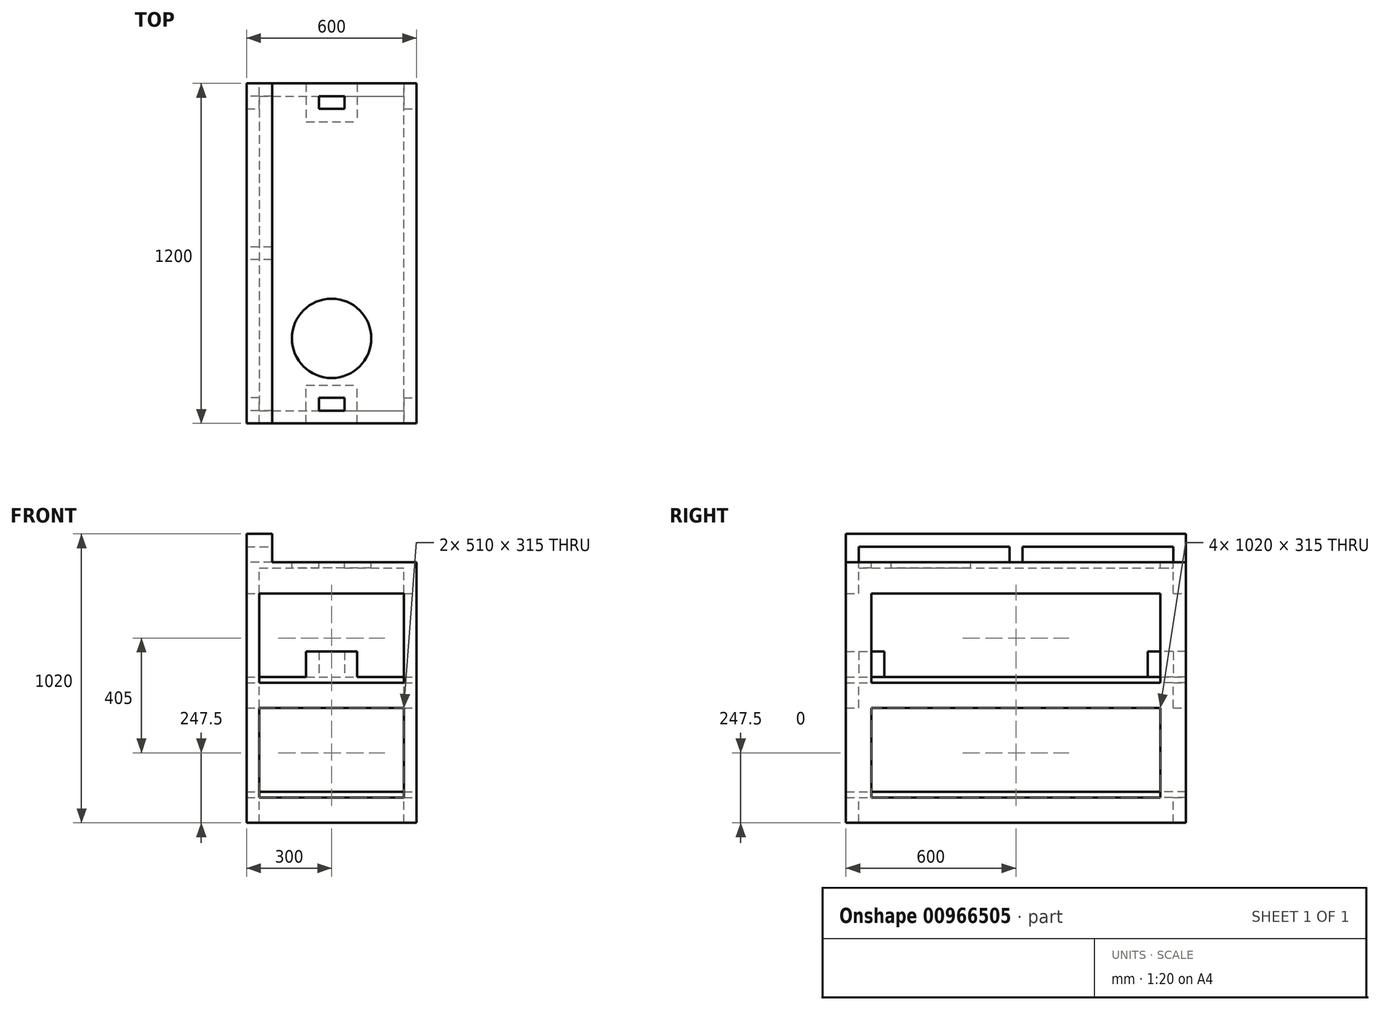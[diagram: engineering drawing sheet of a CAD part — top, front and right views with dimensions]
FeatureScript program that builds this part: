
annotation { "Feature Type Name" : "Feature", "Feature Type Description" : "" }
export const myFeature = defineFeature(function(context is Context, id is Id, definition is map)
    precondition{}
    {
        {
            var Q0;
            Q0=qCreatedBy(makeId("Top.planeOp"),FACE);
            var sketch = newSketch(context, id + "F0", { "sketchPlane" : qUnion([Q0])});
            skLineSegment(sketch, "E0.bottom", {"start": v(0, 0) * mm, "end": v(-600, 0) * mm});
            skLineSegment(sketch, "E0.top", {"start": v(0, 1200) * mm, "end": v(-600, 1200) * mm});
            skLineSegment(sketch, "E0.left", {"start": v(0, 0) * mm, "end": v(0, 1200) * mm});
            skLineSegment(sketch, "E0.right", {"start": v(-600, 0) * mm, "end": v(-600, 1200) * mm});
            skSolve(sketch);
        }
        {
            var Q0;
            Q0 = qSketchRegion(id + "F0", true);
            extrude(context, id + "F1", {"entities" : qUnion([Q0]), "depth" : 900 * mm, "offsetDistance" : 25 * mm});
        }
        {
            var Q0;
            Q0=makeQuery(id+"F1.opExtrude","CAP_FACE",FACE,{"disambiguationData":[OSD([sQuery(id+"F0.wireOp",EDGE,"E0.bottom"),sQuery(id+"F0.wireOp",EDGE,"E0.top"),sQuery(id+"F0.wireOp",EDGE,"E0.left"),sQuery(id+"F0.wireOp",EDGE,"E0.right")])],"isStart":false});
            var sketch = newSketch(context, id + "F2", { "sketchPlane" : qUnion([Q0])});
            skLineSegment(sketch, "E1", {"start": v(0, 600) * mm, "end": v(-600, 600) * mm, "construction": true});
            skLineSegment(sketch, "E2", {"start": v(-300, 0) * mm, "end": v(-300, 1200) * mm, "construction": true});
            skLineSegment(sketch, "E3", {"start": v(-300, 45) * mm, "end": v(-45, 45) * mm});
            skLineSegment(sketch, "E4", {"start": v(-45, 45) * mm, "end": v(-45, 600) * mm});
            skLineSegment(sketch, "E5.MirrorCS", {"start": v(-300, 1155) * mm, "end": v(-45, 1155) * mm});
            skLineSegment(sketch, "E6.MirrorCS", {"start": v(-45, 1155) * mm, "end": v(-45, 600) * mm});
            skLineSegment(sketch, "E7.MirrorCS", {"start": v(-300, 1200) * mm, "end": v(-300, 0) * mm, "construction": true});
            skLineSegment(sketch, "E8.MirrorCS", {"start": v(-300, 1155) * mm, "end": v(-555, 1155) * mm});
            skLineSegment(sketch, "E9.MirrorCS", {"start": v(-555, 1155) * mm, "end": v(-555, 600) * mm});
            skLineSegment(sketch, "E10.MirrorCS", {"start": v(-300, 45) * mm, "end": v(-555, 45) * mm});
            skLineSegment(sketch, "E11.MirrorCS", {"start": v(-555, 45) * mm, "end": v(-555, 600) * mm});
            skSolve(sketch);
        }
        {
            var Q0;
            Q0 = qSketchRegion(id + "F2", true);
            extrude(context, id + "F3", {"entities" : qUnion([Q0]), "operationType" : NewBodyOperationType.REMOVE, "endBound" : BoundingType.THROUGH_ALL, "oppositeDirection" : true, "depth" : 25 * mm, "offsetDistance" : 25 * mm});
        }
        {
            var Q0;
            Q0=makeQuery(id+"F1.opExtrude","SWEPT_FACE",FACE,{"disambiguationData":[OSD([sQuery(id+"F0.wireOp",EDGE,"E0.left")])]});
            var sketch = newSketch(context, id + "F4", { "sketchPlane" : qUnion([Q0])});
            skLineSegment(sketch, "E12.bottom", {"start": v(90, 810) * mm, "end": v(1110, 810) * mm});
            skLineSegment(sketch, "E12.top", {"start": v(90, 495) * mm, "end": v(1110, 495) * mm});
            skLineSegment(sketch, "E12.left", {"start": v(90, 810) * mm, "end": v(90, 495) * mm});
            skLineSegment(sketch, "E12.right", {"start": v(1110, 810) * mm, "end": v(1110, 495) * mm});
            skLineSegment(sketch, "E13.bottom", {"start": v(90, 405) * mm, "end": v(1110, 405) * mm});
            skLineSegment(sketch, "E13.top", {"start": v(90, 90) * mm, "end": v(1110, 90) * mm});
            skLineSegment(sketch, "E13.left", {"start": v(90, 405) * mm, "end": v(90, 90) * mm});
            skLineSegment(sketch, "E13.right", {"start": v(1110, 405) * mm, "end": v(1110, 90) * mm});
            skSolve(sketch);
        }
        {
            var Q0;
            Q0 = qSketchRegion(id + "F4", true);
            extrude(context, id + "F5", {"entities" : qUnion([Q0]), "operationType" : NewBodyOperationType.REMOVE, "endBound" : BoundingType.THROUGH_ALL, "oppositeDirection" : true, "depth" : 25 * mm, "offsetDistance" : 25 * mm});
        }
        {
            var Q0;
            Q0=makeQuery(id+"F1.opExtrude","SWEPT_FACE",FACE,{"disambiguationData":[OSD([sQuery(id+"F0.wireOp",EDGE,"E0.top")])]});
            var sketch = newSketch(context, id + "F6", { "sketchPlane" : qUnion([Q0])});
            skLineSegment(sketch, "E14.bottom", {"start": v(45, 810) * mm, "end": v(555, 810) * mm});
            skLineSegment(sketch, "E14.top", {"start": v(45, 495) * mm, "end": v(555, 495) * mm});
            skLineSegment(sketch, "E14.left", {"start": v(45, 810) * mm, "end": v(45, 495) * mm});
            skLineSegment(sketch, "E14.right", {"start": v(555, 810) * mm, "end": v(555, 495) * mm});
            skLineSegment(sketch, "E15.bottom", {"start": v(45, 405) * mm, "end": v(555, 405) * mm});
            skLineSegment(sketch, "E15.top", {"start": v(45, 90) * mm, "end": v(555, 90) * mm});
            skLineSegment(sketch, "E15.left", {"start": v(45, 405) * mm, "end": v(45, 90) * mm});
            skLineSegment(sketch, "E15.right", {"start": v(555, 405) * mm, "end": v(555, 90) * mm});
            skSolve(sketch);
        }
        {
            var Q0;
            Q0 = qSketchRegion(id + "F6", true);
            extrude(context, id + "F7", {"entities" : qUnion([Q0]), "operationType" : NewBodyOperationType.REMOVE, "endBound" : BoundingType.THROUGH_ALL, "oppositeDirection" : true, "depth" : 25 * mm, "offsetDistance" : 25 * mm});
        }
        {
            var Q0;
            Q0=makeQuery(id+"F1.opExtrude","CAP_FACE",FACE,{"disambiguationData":[OSD([sQuery(id+"F0.wireOp",EDGE,"E0.bottom"),sQuery(id+"F0.wireOp",EDGE,"E0.top"),sQuery(id+"F0.wireOp",EDGE,"E0.left"),sQuery(id+"F0.wireOp",EDGE,"E0.right")])],"isStart":false});
            var sketch = newSketch(context, id + "F8", { "sketchPlane" : qUnion([Q0])});
            skLineSegment(sketch, "E16.bottom", {"start": v(0, 0) * mm, "end": v(-600, 0) * mm});
            skLineSegment(sketch, "E16.top", {"start": v(0, 1200) * mm, "end": v(-600, 1200) * mm});
            skLineSegment(sketch, "E16.left", {"start": v(0, 0) * mm, "end": v(0, 1200) * mm});
            skLineSegment(sketch, "E16.right", {"start": v(-600, 0) * mm, "end": v(-600, 1200) * mm});
            skSolve(sketch);
        }
        {
            var Q0;
            Q0 = qSketchRegion(id + "F8", true);
            extrude(context, id + "F9", {"entities" : qUnion([Q0]), "depth" : 20 * mm, "offsetDistance" : 25 * mm});
        }
        {
            var Q0;
            Q0=makeQuery(id+"F5.boolean.opBoolean","COPY",FACE,{"disambiguationData":[TD([makeQuery(id+"F1.opExtrude","SWEPT_FACE",FACE,{"disambiguationData":[OSD([sQuery(id+"F0.wireOp",EDGE,"E0.left")])]})])],"derivedFrom":makeQuery(id+"F5.opExtrude","SWEPT_FACE",FACE,{"disambiguationData":[OSD([sQuery(id+"F4.wireOp",EDGE,"E12.top")])]})});
            var sketch = newSketch(context, id + "F10", { "sketchPlane" : qUnion([Q0])});
            skLineSegment(sketch, "E17", {"start": v(0, 90) * mm, "end": v(-45, 90) * mm});
            skLineSegment(sketch, "E18", {"start": v(-45, 90) * mm, "end": v(-45, 0) * mm});
            skLineSegment(sketch, "E19", {"start": v(-45, 0) * mm, "end": v(-555, 0) * mm});
            skLineSegment(sketch, "E20", {"start": v(-555, 0) * mm, "end": v(-555, 90) * mm});
            skLineSegment(sketch, "E21", {"start": v(-555, 90) * mm, "end": v(-600, 90) * mm});
            skLineSegment(sketch, "E22", {"start": v(-600, 90) * mm, "end": v(-600, 1110) * mm});
            skLineSegment(sketch, "E23", {"start": v(-600, 1110) * mm, "end": v(-555, 1110) * mm});
            skLineSegment(sketch, "E24", {"start": v(-555, 1110) * mm, "end": v(-555, 1200) * mm});
            skLineSegment(sketch, "E25", {"start": v(-555, 1200) * mm, "end": v(-45, 1200) * mm});
            skLineSegment(sketch, "E26", {"start": v(-45, 1200) * mm, "end": v(-45, 1110) * mm});
            skLineSegment(sketch, "E27", {"start": v(-45, 1110) * mm, "end": v(0, 1110) * mm});
            skLineSegment(sketch, "E28", {"start": v(0, 1110) * mm, "end": v(0, 90) * mm});
            skSolve(sketch);
        }
        {
            var Q0;
            Q0 = qSketchRegion(id + "F10", true);
            extrude(context, id + "F11", {"entities" : qUnion([Q0]), "depth" : 20 * mm, "offsetDistance" : 25 * mm});
        }
        {
            var Q0;
            Q0=makeQuery(id+"F5.boolean.opBoolean","COPY",FACE,{"disambiguationData":[TD([makeQuery(id+"F1.opExtrude","SWEPT_FACE",FACE,{"disambiguationData":[OSD([sQuery(id+"F0.wireOp",EDGE,"E0.left")])]})])],"derivedFrom":makeQuery(id+"F5.opExtrude","SWEPT_FACE",FACE,{"disambiguationData":[OSD([sQuery(id+"F4.wireOp",EDGE,"E13.top")])]})});
            var sketch = newSketch(context, id + "F12", { "sketchPlane" : qUnion([Q0])});
            skLineSegment(sketch, "E29", {"start": v(0, 90) * mm, "end": v(-45, 90) * mm});
            skLineSegment(sketch, "E30", {"start": v(-45, 90) * mm, "end": v(-45, 0) * mm});
            skLineSegment(sketch, "E31", {"start": v(-45, 0) * mm, "end": v(-555, 0) * mm});
            skLineSegment(sketch, "E32", {"start": v(-555, 0) * mm, "end": v(-555, 90) * mm});
            skLineSegment(sketch, "E33", {"start": v(-555, 90) * mm, "end": v(-600, 90) * mm});
            skLineSegment(sketch, "E34", {"start": v(-600, 90) * mm, "end": v(-600, 1110) * mm});
            skLineSegment(sketch, "E35", {"start": v(-600, 1110) * mm, "end": v(-555, 1110) * mm});
            skLineSegment(sketch, "E36", {"start": v(-555, 1110) * mm, "end": v(-555, 1200) * mm});
            skLineSegment(sketch, "E37", {"start": v(-555, 1200) * mm, "end": v(-45, 1200) * mm});
            skLineSegment(sketch, "E38", {"start": v(-45, 1200) * mm, "end": v(-45, 1110) * mm});
            skLineSegment(sketch, "E39", {"start": v(-45, 1110) * mm, "end": v(0, 1110) * mm});
            skLineSegment(sketch, "E40", {"start": v(0, 1110) * mm, "end": v(0, 90) * mm});
            skSolve(sketch);
        }
        {
            var Q0;
            Q0 = qSketchRegion(id + "F12", true);
            extrude(context, id + "F13", {"entities" : qUnion([Q0]), "depth" : 20 * mm, "offsetDistance" : 25 * mm});
        }
        {
            var Q0;
            Q0=makeQuery(id+"F9.opExtrude","CAP_FACE",FACE,{"disambiguationData":[OSD([sQuery(id+"F8.wireOp",EDGE,"E16.bottom"),sQuery(id+"F8.wireOp",EDGE,"E16.top"),sQuery(id+"F8.wireOp",EDGE,"E16.left"),sQuery(id+"F8.wireOp",EDGE,"E16.right")])],"isStart":false});
            var sketch = newSketch(context, id + "F14", { "sketchPlane" : qUnion([Q0])});
            skCircle(sketch, "E41", {"center": v(-300, 300) * mm, "radius": 140 * mm});
            skSolve(sketch);
        }
        {
            var Q0;
            Q0 = qSketchRegion(id + "F14", true);
            extrude(context, id + "F15", {"entities" : qUnion([Q0]), "operationType" : NewBodyOperationType.REMOVE, "endBound" : BoundingType.UP_TO_NEXT, "oppositeDirection" : true, "depth" : 25 * mm, "offsetDistance" : 25 * mm});
        }
        {
            var Q0;
            Q0=makeQuery(id+"F9.opExtrude","CAP_FACE",FACE,{"disambiguationData":[OSD([sQuery(id+"F8.wireOp",EDGE,"E16.bottom"),sQuery(id+"F8.wireOp",EDGE,"E16.top"),sQuery(id+"F8.wireOp",EDGE,"E16.left"),sQuery(id+"F8.wireOp",EDGE,"E16.right")])],"isStart":false});
            var sketch = newSketch(context, id + "F16", { "sketchPlane" : qUnion([Q0])});
            skLineSegment(sketch, "E42", {"start": v(-600, 600) * mm, "end": v(0, 600) * mm, "construction": true});
            skLineSegment(sketch, "E43.bottom", {"start": v(-345, 45) * mm, "end": v(-255, 45) * mm});
            skLineSegment(sketch, "E43.top", {"start": v(-345, 90) * mm, "end": v(-255, 90) * mm});
            skLineSegment(sketch, "E43.left", {"start": v(-345, 45) * mm, "end": v(-345, 90) * mm});
            skLineSegment(sketch, "E43.right", {"start": v(-255, 45) * mm, "end": v(-255, 90) * mm});
            skPoint(sketch, "E44", {"position": v(-300, 45) * mm});
            skLineSegment(sketch, "E45.MirrorCS", {"start": v(-345, 1155) * mm, "end": v(-255, 1155) * mm});
            skPoint(sketch, "E46.MirrorP", {"position": v(-300, 1155) * mm});
            skLineSegment(sketch, "E47.MirrorCS", {"start": v(-345, 1155) * mm, "end": v(-345, 1110) * mm});
            skLineSegment(sketch, "E48.MirrorCS", {"start": v(-255, 1155) * mm, "end": v(-255, 1110) * mm});
            skLineSegment(sketch, "E49.MirrorCS", {"start": v(-345, 1110) * mm, "end": v(-255, 1110) * mm});
            skSolve(sketch);
        }
        {
            var Q0;
            Q0 = qSketchRegion(id + "F16", true);
            extrude(context, id + "F17", {"entities" : qUnion([Q0]), "operationType" : NewBodyOperationType.REMOVE, "endBound" : BoundingType.UP_TO_NEXT, "oppositeDirection" : true, "depth" : 25 * mm, "offsetDistance" : 25 * mm});
        }
        {
            var Q0;
            Q0=makeQuery(id+"F11.opExtrude","CAP_FACE",FACE,{"disambiguationData":[OSD([sQuery(id+"F10.wireOp",EDGE,"E17"),sQuery(id+"F10.wireOp",EDGE,"E18"),sQuery(id+"F10.wireOp",EDGE,"E19"),sQuery(id+"F10.wireOp",EDGE,"E20"),sQuery(id+"F10.wireOp",EDGE,"E21"),sQuery(id+"F10.wireOp",EDGE,"E22"),sQuery(id+"F10.wireOp",EDGE,"E23"),sQuery(id+"F10.wireOp",EDGE,"E24"),sQuery(id+"F10.wireOp",EDGE,"E25"),sQuery(id+"F10.wireOp",EDGE,"E26"),sQuery(id+"F10.wireOp",EDGE,"E27"),sQuery(id+"F10.wireOp",EDGE,"E28")])],"isStart":false});
            var sketch = newSketch(context, id + "F18", { "sketchPlane" : qUnion([Q0])});
            skLineSegment(sketch, "E50.bottom", {"start": v(-345, 45) * mm, "end": v(-255, 45) * mm});
            skLineSegment(sketch, "E50.top", {"start": v(-345, 90) * mm, "end": v(-255, 90) * mm});
            skLineSegment(sketch, "E50.left", {"start": v(-345, 45) * mm, "end": v(-345, 90) * mm});
            skLineSegment(sketch, "E50.right", {"start": v(-255, 45) * mm, "end": v(-255, 90) * mm});
            skPoint(sketch, "E51", {"position": v(-300, 45) * mm});
            skPoint(sketch, "E52", {"position": v(-300, 0) * mm});
            skLineSegment(sketch, "E53.bottom", {"start": v(-390, 0) * mm, "end": v(-210, 0) * mm});
            skLineSegment(sketch, "E53.top", {"start": v(-390, 135) * mm, "end": v(-210, 135) * mm});
            skLineSegment(sketch, "E53.left", {"start": v(-390, 0) * mm, "end": v(-390, 135) * mm});
            skLineSegment(sketch, "E53.right", {"start": v(-210, 0) * mm, "end": v(-210, 135) * mm});
            skLineSegment(sketch, "E54", {"start": v(0, 600) * mm, "end": v(-600, 600) * mm, "construction": true});
            skPoint(sketch, "E55.MirrorP", {"position": v(-300, 1155) * mm});
            skLineSegment(sketch, "E56.MirrorCS", {"start": v(-210, 1200) * mm, "end": v(-210, 1065) * mm});
            skLineSegment(sketch, "E57.MirrorCS", {"start": v(-345, 1155) * mm, "end": v(-345, 1110) * mm});
            skLineSegment(sketch, "E58.MirrorCS", {"start": v(-390, 1065) * mm, "end": v(-210, 1065) * mm});
            skLineSegment(sketch, "E59.MirrorCS", {"start": v(-345, 1155) * mm, "end": v(-255, 1155) * mm});
            skLineSegment(sketch, "E60.MirrorCS", {"start": v(-390, 1200) * mm, "end": v(-210, 1200) * mm});
            skPoint(sketch, "E61.MirrorP", {"position": v(-300, 1200) * mm});
            skLineSegment(sketch, "E62.MirrorCS", {"start": v(-390, 1200) * mm, "end": v(-390, 1065) * mm});
            skLineSegment(sketch, "E63.MirrorCS", {"start": v(-345, 1110) * mm, "end": v(-255, 1110) * mm});
            skLineSegment(sketch, "E64.MirrorCS", {"start": v(-255, 1155) * mm, "end": v(-255, 1110) * mm});
            skSolve(sketch);
        }
        {
            var Q0;
            Q0 = qSketchRegion(id + "F18", true);
            extrude(context, id + "F19", {"entities" : qUnion([Q0]), "operationType" : NewBodyOperationType.ADD, "depth" : 90 * mm, "offsetDistance" : 25 * mm});
        }
        {
            var Q0;
            Q0=makeQuery(id+"F1.opExtrude","CAP_FACE",FACE,{"disambiguationData":[OSD([sQuery(id+"F0.wireOp",EDGE,"E0.bottom"),sQuery(id+"F0.wireOp",EDGE,"E0.top"),sQuery(id+"F0.wireOp",EDGE,"E0.left"),sQuery(id+"F0.wireOp",EDGE,"E0.right")])],"isStart":false});
            var sketch = newSketch(context, id + "F20", { "sketchPlane" : qUnion([Q0])});
            skLineSegment(sketch, "E65.bottom", {"start": v(-600, 0) * mm, "end": v(-510, 0) * mm});
            skLineSegment(sketch, "E65.top", {"start": v(-600, 45) * mm, "end": v(-510, 45) * mm});
            skLineSegment(sketch, "E65.left", {"start": v(-600, 0) * mm, "end": v(-600, 45) * mm});
            skLineSegment(sketch, "E65.right", {"start": v(-510, 0) * mm, "end": v(-510, 45) * mm});
            skLineSegment(sketch, "E66.bottom", {"start": v(-600, 1200) * mm, "end": v(-510, 1200) * mm});
            skLineSegment(sketch, "E66.top", {"start": v(-600, 1155) * mm, "end": v(-510, 1155) * mm});
            skLineSegment(sketch, "E66.left", {"start": v(-600, 1200) * mm, "end": v(-600, 1155) * mm});
            skLineSegment(sketch, "E66.right", {"start": v(-510, 1200) * mm, "end": v(-510, 1155) * mm});
            skLineSegment(sketch, "E67.bottom", {"start": v(-600, 577.5) * mm, "end": v(-510, 577.5) * mm});
            skLineSegment(sketch, "E67.top", {"start": v(-600, 622.5) * mm, "end": v(-510, 622.5) * mm});
            skLineSegment(sketch, "E67.left", {"start": v(-600, 577.5) * mm, "end": v(-600, 622.5) * mm});
            skLineSegment(sketch, "E67.right", {"start": v(-510, 577.5) * mm, "end": v(-510, 622.5) * mm});
            skPoint(sketch, "E68", {"position": v(-510, 600) * mm});
            skLineSegment(sketch, "E69", {"start": v(-600, 600) * mm, "end": v(-510, 600) * mm, "construction": true});
            skSolve(sketch);
        }
        {
            var Q0;
            Q0 = qSketchRegion(id + "F20", true);
            extrude(context, id + "F21", {"entities" : qUnion([Q0]), "operationType" : NewBodyOperationType.ADD, "depth" : 75 * mm, "offsetDistance" : 25 * mm});
        }
        {
            var Q0;
            Q0=makeQuery(id+"F21.opExtrude","CAP_FACE",FACE,{"disambiguationData":[OSD([sQuery(id+"F20.wireOp",EDGE,"E65.bottom"),sQuery(id+"F20.wireOp",EDGE,"E65.top"),sQuery(id+"F20.wireOp",EDGE,"E65.left"),sQuery(id+"F20.wireOp",EDGE,"E65.right")])],"isStart":false});
            var sketch = newSketch(context, id + "F22", { "sketchPlane" : qUnion([Q0])});
            skLineSegment(sketch, "E70.bottom", {"start": v(-600, 0) * mm, "end": v(-510, 0) * mm});
            skLineSegment(sketch, "E70.top", {"start": v(-600, 1200) * mm, "end": v(-510, 1200) * mm});
            skLineSegment(sketch, "E70.left", {"start": v(-600, 0) * mm, "end": v(-600, 1200) * mm});
            skLineSegment(sketch, "E70.right", {"start": v(-510, 0) * mm, "end": v(-510, 1200) * mm});
            skSolve(sketch);
        }
        {
            var Q0;
            Q0 = qSketchRegion(id + "F22", true);
            extrude(context, id + "F23", {"entities" : qUnion([Q0]), "operationType" : NewBodyOperationType.ADD, "depth" : 45 * mm, "offsetDistance" : 25 * mm});
        }
    });
